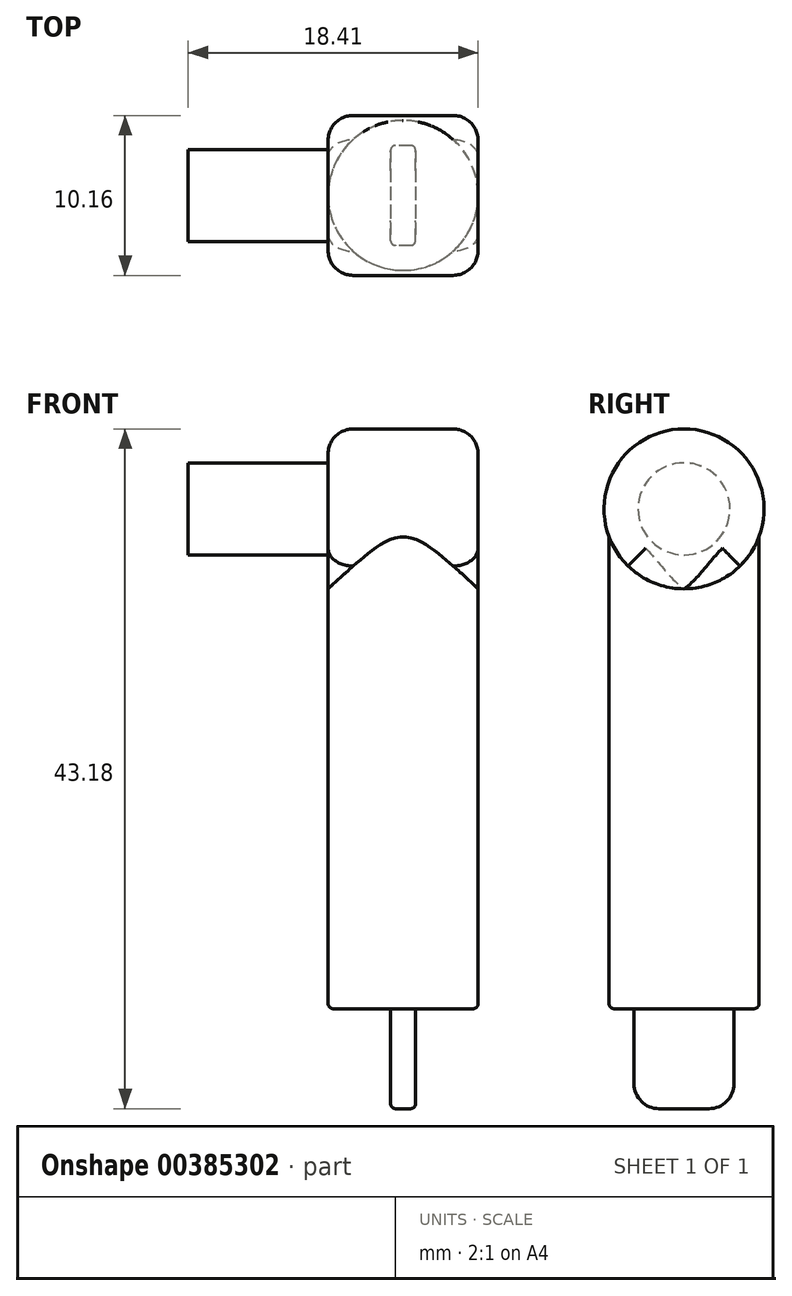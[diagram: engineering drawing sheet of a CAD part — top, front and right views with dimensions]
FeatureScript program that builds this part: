
annotation { "Feature Type Name" : "Feature", "Feature Type Description" : "" }
export const myFeature = defineFeature(function(context is Context, id is Id, definition is map)
    precondition{}
    {
        {
            var Q0;
            Q0=qCreatedBy(makeId("Top.planeOp"),FACE);
            var sketch = newSketch(context, id + "F0", { "sketchPlane" : qUnion([Q0])});
            skCircle(sketch, "E0", {"center": v(0, 0) * mm, "radius": 4.76 * mm});
            skSolve(sketch);
        }
        {
            var Q0;
            Q0 = qSketchRegion(id + "F0", true);
            extrude(context, id + "F1", {"entities" : qUnion([Q0]), "depth" : 31.75 * mm});
        }
        {
            var Q0;
            Q0=qCreatedBy(makeId("Right.planeOp"),FACE);
            var sketch = newSketch(context, id + "F2", { "sketchPlane" : qUnion([Q0])});
            skLineSegment(sketch, "E1", {"start": v(3.17, 0) * mm, "end": v(-3.18, 0) * mm});
            skLineSegment(sketch, "E2", {"start": v(-3.18, 0) * mm, "end": v(-3.17, -4.76) * mm});
            skLineSegment(sketch, "E3", {"start": v(3.17, 0) * mm, "end": v(3.18, -4.76) * mm});
            skLineSegment(sketch, "E4", {"start": v(1.59, -6.35) * mm, "end": v(-1.59, -6.35) * mm});
            skPoint(sketch, "E5.visualSharp", {"position": v(3.18, -6.35) * mm});
            skArc(sketch, "E5.filletArc", {"start": v(1.59, -6.35) * mm, "mid": v(2.71, -5.89) * mm, "end": v(3.18, -4.76) * mm});
            skPoint(sketch, "E6.visualSharp", {"position": v(-3.17, -6.35) * mm});
            skArc(sketch, "E6.filletArc", {"start": v(-3.18, -4.76) * mm, "mid": v(-2.71, -5.89) * mm, "end": v(-1.59, -6.35) * mm});
            skSolve(sketch);
        }
        {
            var Q0;
            Q0 = qSketchRegion(id + "F2", true);
            extrude(context, id + "F3", {"entities" : qUnion([Q0]), "operationType" : NewBodyOperationType.ADD, "endBound" : BoundingType.SYMMETRIC, "depth" : 1.59 * mm});
        }
        {
            var Q0;
            Q0=makeQuery(id+"F1.opExtrude","CAP_EDGE",EDGE,{"disambiguationData":[OSD([sQuery(id+"F0.wireOp",EDGE,"E0")])],"isStart":true});
            fillet(context, id + "F4", {"entities" : qUnion([Q0]), "radius" : 0.32 * mm, "tangentPropagation" : true, "allowEdgeOverflow" : false});
        }
        {
            var Q0;
            Q0=makeQuery(id+"F3.opExtrude","CAP_EDGE",EDGE,{"disambiguationData":[OSD([sQuery(id+"F2.wireOp",EDGE,"E2")])],"isStart":true});
            var Q1;
            Q1=makeQuery(id+"F3.opExtrude","CAP_EDGE",EDGE,{"disambiguationData":[OSD([sQuery(id+"F2.wireOp",EDGE,"E6.filletArc")])],"isStart":true});
            var Q2;
            Q2=makeQuery(id+"F3.opExtrude","CAP_EDGE",EDGE,{"disambiguationData":[OSD([sQuery(id+"F2.wireOp",EDGE,"E2")])],"isStart":false});
            var Q3;
            Q3=makeQuery(id+"F3.opExtrude","CAP_EDGE",EDGE,{"disambiguationData":[OSD([sQuery(id+"F2.wireOp",EDGE,"E6.filletArc")])],"isStart":false});
            var Q4;
            Q4=makeQuery(id+"F3.opExtrude","CAP_EDGE",EDGE,{"disambiguationData":[OSD([sQuery(id+"F2.wireOp",EDGE,"E4")])],"isStart":true});
            var Q5;
            Q5=makeQuery(id+"F3.opExtrude","CAP_EDGE",EDGE,{"disambiguationData":[OSD([sQuery(id+"F2.wireOp",EDGE,"E5.filletArc")])],"isStart":true});
            var Q6;
            Q6=makeQuery(id+"F3.opExtrude","CAP_EDGE",EDGE,{"disambiguationData":[OSD([sQuery(id+"F2.wireOp",EDGE,"E3")])],"isStart":true});
            var Q7;
            Q7=makeQuery(id+"F3.opExtrude","CAP_EDGE",EDGE,{"disambiguationData":[OSD([sQuery(id+"F2.wireOp",EDGE,"E3")])],"isStart":false});
            var Q8;
            Q8=makeQuery(id+"F3.opExtrude","CAP_EDGE",EDGE,{"disambiguationData":[OSD([sQuery(id+"F2.wireOp",EDGE,"E5.filletArc")])],"isStart":false});
            var Q9;
            Q9=makeQuery(id+"F3.opExtrude","CAP_EDGE",EDGE,{"disambiguationData":[OSD([sQuery(id+"F2.wireOp",EDGE,"E4")])],"isStart":false});
            fillet(context, id + "F5", {"entities" : qUnion([Q0, Q1, Q2, Q3, Q4, Q5, Q6, Q7, Q8, Q9]), "radius" : 0.32 * mm, "tangentPropagation" : true, "allowEdgeOverflow" : false});
        }
        {
            var Q0;
            Q0=qCreatedBy(makeId("Right.planeOp"),FACE);
            var sketch = newSketch(context, id + "F6", { "sketchPlane" : qUnion([Q0])});
            skCircle(sketch, "E7", {"center": v(0, 31.75) * mm, "radius": 5.08 * mm});
            skLineSegment(sketch, "E8", {"start": v(5.08, 31.75) * mm, "end": v(-5.08, 31.75) * mm});
            skSolve(sketch);
        }
        {
            var Q0;
            Q0 = qSketchRegion(id + "F6", true);
            extrude(context, id + "F7", {"entities" : qUnion([Q0]), "operationType" : NewBodyOperationType.ADD, "endBound" : BoundingType.SYMMETRIC, "depth" : 9.52 * mm});
        }
        {
            var Q0;
            Q0=makeQuery(id+"F7.opExtrude","CAP_FACE",FACE,{"disambiguationData":[OSD([sQuery(id+"F6.wireOp",EDGE,"E7")])],"isStart":true});
            var sketch = newSketch(context, id + "F8", { "sketchPlane" : qUnion([Q0])});
            skCircle(sketch, "E9", {"center": v(0, 31.75) * mm, "radius": 2.92 * mm});
            skSolve(sketch);
        }
        {
            var Q0;
            Q0 = qSketchRegion(id + "F8", true);
            extrude(context, id + "F9", {"entities" : qUnion([Q0]), "operationType" : NewBodyOperationType.ADD, "depth" : 8.9 * mm});
        }
        {
            var Q0;
            Q0=makeQuery(id+"F7.opExtrude","CAP_EDGE",EDGE,{"disambiguationData":[OSD([sQuery(id+"F6.wireOp",EDGE,"E7")])],"isStart":true});
            var Q1;
            Q1=makeQuery(id+"F7.opExtrude","CAP_EDGE",EDGE,{"disambiguationData":[OSD([sQuery(id+"F6.wireOp",EDGE,"E7")])],"isStart":false});
            fillet(context, id + "F10", {"entities" : qUnion([Q0, Q1]), "radius" : 1.59 * mm, "tangentPropagation" : true, "allowEdgeOverflow" : false});
        }
    });
